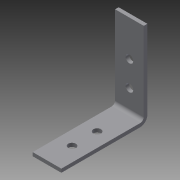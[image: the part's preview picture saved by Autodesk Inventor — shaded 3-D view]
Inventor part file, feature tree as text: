
AUTODESK INVENTOR PART (.ipt)
format: ipt  version: 2013 (Build 170138000, 138)  size: 156,672 bytes
history: native  units: in
note: dims shown in document units (in); Inventor stores cm internally (conversion verified against a paired STEP export)
features: sheet_metal_op x4, other x4, sketch x3
ambient origin geometry x8: Origin, YZ Plane, XZ Plane, XY Plane, X Axis, Y Axis, Z Axis, Center Point
bodies: Solid1 (feature_tree)
feature tree (11):
  sheet_metal_op  "Face1"
  sheet_metal_op  "Flange1"
  sketch  "Sketch1"  dims[d0=3.0in]
  other  "Plate1"
  sketch  "Sketch2"  dims[d1=1.0in]
  other  "Plate2"
  sheet_metal_op  "Bend1"
  sheet_metal_op  "Corner1"
  sketch  "Sketch3"  dims[d3=0.266in d4=0.875in d8=0.266in d10=0.125in d11=0.125in d12=0.0625in d13=0.25in d14=0.125in d15=3.0in d16=90.0deg d17=0.125in d18=0.5in d19=0.125in d20=0.125in d21=0.266in d22=0.266in d23=0.5in d24=0.875in d25=0.875in d26=0.125in d27=0.0in d2=0.25in d5=0.25in d6=0.125in d7=0.0in]
  other  "Cut1"
  other  "Definition1"
